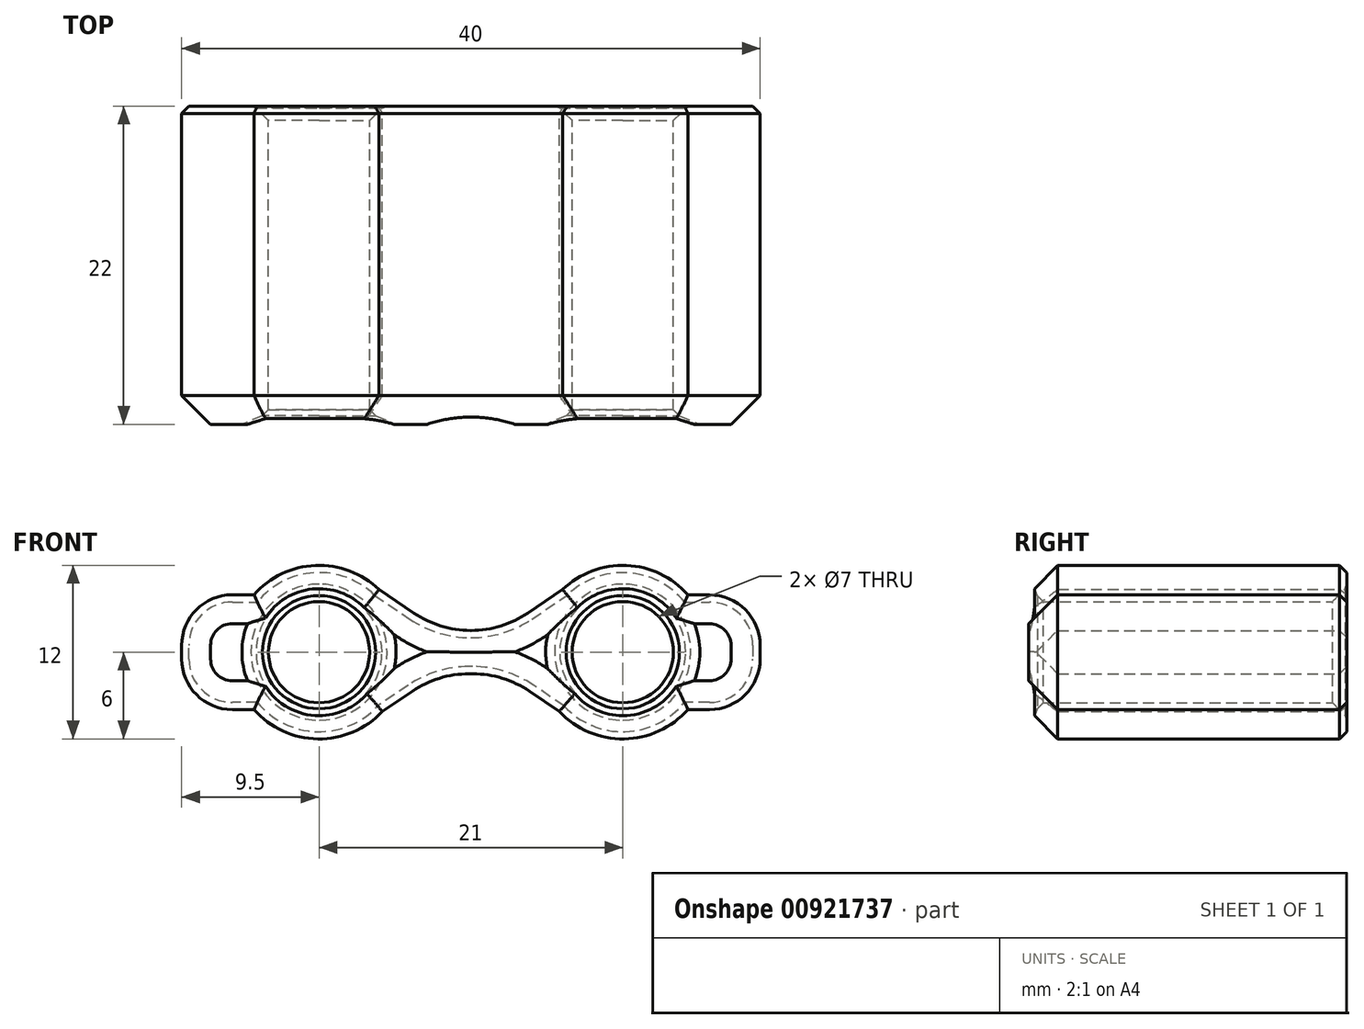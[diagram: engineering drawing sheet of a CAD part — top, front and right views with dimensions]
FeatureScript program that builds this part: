
annotation { "Feature Type Name" : "Feature", "Feature Type Description" : "" }
export const myFeature = defineFeature(function(context is Context, id is Id, definition is map)
    precondition{}
    {
        {
            var Q0;
            Q0=qCreatedBy(makeId("Front.planeOp"),FACE);
            var sketch = newSketch(context, id + "F0", { "sketchPlane" : qUnion([Q0])});
            skPoint(sketch, "E0.middle", {"position": v(0, 0) * mm});
            skArc(sketch, "E1", {"start": v(-15, -3.97) * mm, "mid": v(-10.59, -6) * mm, "end": v(-6.12, -4.1) * mm});
            skArc(sketch, "E2", {"start": v(15, 3.96) * mm, "mid": v(10.76, 6) * mm, "end": v(6.35, 4.33) * mm});
            skLineSegment(sketch, "E3", {"start": v(-15, 3.97) * mm, "end": v(-20, 3.97) * mm});
            skLineSegment(sketch, "E4", {"start": v(-15, -3.97) * mm, "end": v(-20, -3.97) * mm});
            skLineSegment(sketch, "E5", {"start": v(-20, -3.97) * mm, "end": v(-20, 3.97) * mm});
            skLineSegment(sketch, "E6", {"start": v(15, 3.96) * mm, "end": v(20, 3.96) * mm});
            skLineSegment(sketch, "E7", {"start": v(15, -3.97) * mm, "end": v(20, -3.97) * mm});
            skLineSegment(sketch, "E8", {"start": v(20, -3.97) * mm, "end": v(20, 3.96) * mm});
            skCircle(sketch, "E9", {"center": v(-10.5, 0) * mm, "radius": 3.5 * mm});
            skCircle(sketch, "E10", {"center": v(10.5, 0) * mm, "radius": 3.5 * mm});
            skArc(sketch, "E11.trimOffspring", {"start": v(-6.35, 4.33) * mm, "mid": v(-10.75, 6) * mm, "end": v(-15, 3.97) * mm});
            skArc(sketch, "E12.trimOffspring", {"start": v(6.12, -4.1) * mm, "mid": v(10.59, -6) * mm, "end": v(15, -3.97) * mm});
            skLineSegment(sketch, "E13.trimOffspring", {"start": v(2.27, -1.5) * mm, "end": v(-2.27, -1.5) * mm});
            skPoint(sketch, "E14.left.end.orphan", {"position": v(8.46, -1.5) * mm});
            skLineSegment(sketch, "E15.trimOffspring", {"start": v(2.16, 1.5) * mm, "end": v(-2.16, 1.5) * mm});
            skPoint(sketch, "E14.right.end.orphan", {"position": v(-8.46, -1.5) * mm});
            skPoint(sketch, "E14.right.start.orphan", {"position": v(-8.46, 1.5) * mm});
            skPoint(sketch, "E14.bottom.start.orphan", {"position": v(8.46, 1.5) * mm});
            skLineSegment(sketch, "E16", {"start": v(-6.35, 4.33) * mm, "end": v(-2.16, 1.5) * mm});
            skLineSegment(sketch, "E17", {"start": v(6.35, 4.33) * mm, "end": v(2.16, 1.5) * mm});
            skLineSegment(sketch, "E18.trimOffspring", {"start": v(2.27, -1.5) * mm, "end": v(6.12, -4.1) * mm});
            skLineSegment(sketch, "E19.trimOffspring", {"start": v(-2.27, -1.5) * mm, "end": v(-6.12, -4.1) * mm});
            skSolve(sketch);
        }
        {
            var Q0;
            Q0=makeQuery(id+"F0.imprint","IMPRINT",FACE,{"disambiguationData":[TD([[makeQuery(id+"F0.imprint","IMPRINT",EDGE,{"derivedFrom":sQuery(id+"F0.wireOp",EDGE,"E1")}),1.0]])]});
            extrude(context, id + "F1", {"entities" : qUnion([Q0]), "depth" : 22 * mm, "offsetDistance" : 25 * mm});
        }
        {
            var Q0;
            Q0=makeQuery(id+"F1.opExtrude","CAP_EDGE",EDGE,{"disambiguationData":[OSD([sQuery(id+"F0.wireOp",EDGE,"E9")])],"isStart":false});
            var Q1;
            Q1=makeQuery(id+"F1.opExtrude","CAP_EDGE",EDGE,{"disambiguationData":[OSD([sQuery(id+"F0.wireOp",EDGE,"E10")])],"isStart":false});
            var Q2;
            Q2=makeQuery(id+"F1.opExtrude","CAP_EDGE",EDGE,{"disambiguationData":[OSD([sQuery(id+"F0.wireOp",EDGE,"E9")])],"isStart":true});
            var Q3;
            Q3=makeQuery(id+"F1.opExtrude","CAP_EDGE",EDGE,{"disambiguationData":[OSD([sQuery(id+"F0.wireOp",EDGE,"E10")])],"isStart":true});
            chamfer(context, id + "F2", {"entities" : qUnion([Q0, Q1, Q2, Q3]), "width" : 1 * mm, "tangentPropagation" : true});
        }
        {
            var Q0;
            Q0=makeQuery(id+"F1.opExtrude","SWEPT_EDGE",EDGE,{"disambiguationData":[OSD([sQuery(id+"F0.wireOp",EDGE,"E3"),sQuery(id+"F0.wireOp",EDGE,"E5")])]});
            var Q1;
            Q1=makeQuery(id+"F1.opExtrude","SWEPT_EDGE",EDGE,{"disambiguationData":[OSD([sQuery(id+"F0.wireOp",EDGE,"E4"),sQuery(id+"F0.wireOp",EDGE,"E5")])]});
            var Q2;
            Q2=makeQuery(id+"F1.opExtrude","SWEPT_EDGE",EDGE,{"disambiguationData":[OSD([sQuery(id+"F0.wireOp",EDGE,"E6"),sQuery(id+"F0.wireOp",EDGE,"E8")])]});
            var Q3;
            Q3=makeQuery(id+"F1.opExtrude","SWEPT_EDGE",EDGE,{"disambiguationData":[OSD([sQuery(id+"F0.wireOp",EDGE,"E7"),sQuery(id+"F0.wireOp",EDGE,"E8")])]});
            fillet(context, id + "F3", {"entities" : qUnion([Q0, Q1, Q2, Q3]), "radius" : 3.5 * mm, "tangentPropagation" : true, "allowEdgeOverflow" : false});
        }
        {
            var Q0;
            Q0=makeQuery(id+"F1.opExtrude","SWEPT_EDGE",EDGE,{"disambiguationData":[OSD([sQuery(id+"F0.wireOp",EDGE,"E15.trimOffspring"),sQuery(id+"F0.wireOp",EDGE,"E16")])]});
            var Q1;
            Q1=makeQuery(id+"F1.opExtrude","SWEPT_EDGE",EDGE,{"disambiguationData":[OSD([sQuery(id+"F0.wireOp",EDGE,"E15.trimOffspring"),sQuery(id+"F0.wireOp",EDGE,"E17")])]});
            var Q2;
            Q2=makeQuery(id+"F1.opExtrude","SWEPT_EDGE",EDGE,{"disambiguationData":[OSD([sQuery(id+"F0.wireOp",EDGE,"E13.trimOffspring"),sQuery(id+"F0.wireOp",EDGE,"E19.trimOffspring")])]});
            var Q3;
            Q3=makeQuery(id+"F1.opExtrude","SWEPT_EDGE",EDGE,{"disambiguationData":[OSD([sQuery(id+"F0.wireOp",EDGE,"E13.trimOffspring"),sQuery(id+"F0.wireOp",EDGE,"E18.trimOffspring")])]});
            fillet(context, id + "F4", {"entities" : qUnion([Q0, Q1, Q2, Q3]), "radius" : 7 * mm, "tangentPropagation" : true, "allowEdgeOverflow" : false});
        }
        {
            var Q0;
            Q0=makeQuery(id+"F1.opExtrude","CAP_FACE",FACE,{"disambiguationData":[OSD([sQuery(id+"F0.wireOp",EDGE,"E1"),sQuery(id+"F0.wireOp",EDGE,"E2"),sQuery(id+"F0.wireOp",EDGE,"E3"),sQuery(id+"F0.wireOp",EDGE,"E4"),sQuery(id+"F0.wireOp",EDGE,"E5"),sQuery(id+"F0.wireOp",EDGE,"E6"),sQuery(id+"F0.wireOp",EDGE,"E7"),sQuery(id+"F0.wireOp",EDGE,"E8"),sQuery(id+"F0.wireOp",EDGE,"E9"),sQuery(id+"F0.wireOp",EDGE,"E10"),sQuery(id+"F0.wireOp",EDGE,"E11.trimOffspring"),sQuery(id+"F0.wireOp",EDGE,"E12.trimOffspring"),sQuery(id+"F0.wireOp",EDGE,"E13.trimOffspring"),sQuery(id+"F0.wireOp",EDGE,"E15.trimOffspring"),sQuery(id+"F0.wireOp",EDGE,"E16"),sQuery(id+"F0.wireOp",EDGE,"E17"),sQuery(id+"F0.wireOp",EDGE,"E18.trimOffspring"),sQuery(id+"F0.wireOp",EDGE,"E19.trimOffspring")])],"isStart":false});
            chamfer(context, id + "F5", {"entities" : qUnion([Q0]), "width" : 2 * mm, "tangentPropagation" : true});
        }
        {
            var Q0;
            {var subQ0=sQuery(id+"F0.wireOp",EDGE,"E8");var subQ1=sQuery(id+"F0.wireOp",EDGE,"E6");Q0=makeQuery(id+"F3.opFillet","BLEND_EDGE",EDGE,{"blendedFrom":[makeQuery(id+"F1.opExtrude","SWEPT_EDGE",EDGE,{"disambiguationData":[OSD([subQ1,subQ0])]}),makeQuery(id+"F1.opExtrude","CAP_FACE",FACE,{"disambiguationData":[OSD([sQuery(id+"F0.wireOp",EDGE,"E1"),sQuery(id+"F0.wireOp",EDGE,"E2"),sQuery(id+"F0.wireOp",EDGE,"E3"),sQuery(id+"F0.wireOp",EDGE,"E4"),sQuery(id+"F0.wireOp",EDGE,"E5"),subQ1,sQuery(id+"F0.wireOp",EDGE,"E7"),subQ0,sQuery(id+"F0.wireOp",EDGE,"E9"),sQuery(id+"F0.wireOp",EDGE,"E10"),sQuery(id+"F0.wireOp",EDGE,"E11.trimOffspring"),sQuery(id+"F0.wireOp",EDGE,"E12.trimOffspring"),sQuery(id+"F0.wireOp",EDGE,"E13.trimOffspring"),sQuery(id+"F0.wireOp",EDGE,"E15.trimOffspring"),sQuery(id+"F0.wireOp",EDGE,"E16"),sQuery(id+"F0.wireOp",EDGE,"E17"),sQuery(id+"F0.wireOp",EDGE,"E18.trimOffspring"),sQuery(id+"F0.wireOp",EDGE,"E19.trimOffspring")])],"isStart":true})],"blendedInto":[makeQuery(id+"F1.opExtrude","CAP_FACE",FACE,{"disambiguationData":[OSD([sQuery(id+"F0.wireOp",EDGE,"E1"),sQuery(id+"F0.wireOp",EDGE,"E2"),sQuery(id+"F0.wireOp",EDGE,"E3"),sQuery(id+"F0.wireOp",EDGE,"E4"),sQuery(id+"F0.wireOp",EDGE,"E5"),subQ1,sQuery(id+"F0.wireOp",EDGE,"E7"),subQ0,sQuery(id+"F0.wireOp",EDGE,"E9"),sQuery(id+"F0.wireOp",EDGE,"E10"),sQuery(id+"F0.wireOp",EDGE,"E11.trimOffspring"),sQuery(id+"F0.wireOp",EDGE,"E12.trimOffspring"),sQuery(id+"F0.wireOp",EDGE,"E13.trimOffspring"),sQuery(id+"F0.wireOp",EDGE,"E15.trimOffspring"),sQuery(id+"F0.wireOp",EDGE,"E16"),sQuery(id+"F0.wireOp",EDGE,"E17"),sQuery(id+"F0.wireOp",EDGE,"E18.trimOffspring"),sQuery(id+"F0.wireOp",EDGE,"E19.trimOffspring")])],"isStart":true})]});}
            var Q1;
            {var subQ0=sQuery(id+"F0.wireOp",EDGE,"E5");var subQ1=sQuery(id+"F0.wireOp",EDGE,"E3");Q1=makeQuery(id+"F3.opFillet","BLEND_EDGE",EDGE,{"blendedFrom":[makeQuery(id+"F1.opExtrude","SWEPT_EDGE",EDGE,{"disambiguationData":[OSD([subQ1,subQ0])]}),makeQuery(id+"F1.opExtrude","CAP_FACE",FACE,{"disambiguationData":[OSD([sQuery(id+"F0.wireOp",EDGE,"E1"),sQuery(id+"F0.wireOp",EDGE,"E2"),subQ1,sQuery(id+"F0.wireOp",EDGE,"E4"),subQ0,sQuery(id+"F0.wireOp",EDGE,"E6"),sQuery(id+"F0.wireOp",EDGE,"E7"),sQuery(id+"F0.wireOp",EDGE,"E8"),sQuery(id+"F0.wireOp",EDGE,"E9"),sQuery(id+"F0.wireOp",EDGE,"E10"),sQuery(id+"F0.wireOp",EDGE,"E11.trimOffspring"),sQuery(id+"F0.wireOp",EDGE,"E12.trimOffspring"),sQuery(id+"F0.wireOp",EDGE,"E13.trimOffspring"),sQuery(id+"F0.wireOp",EDGE,"E15.trimOffspring"),sQuery(id+"F0.wireOp",EDGE,"E16"),sQuery(id+"F0.wireOp",EDGE,"E17"),sQuery(id+"F0.wireOp",EDGE,"E18.trimOffspring"),sQuery(id+"F0.wireOp",EDGE,"E19.trimOffspring")])],"isStart":true})],"blendedInto":[makeQuery(id+"F1.opExtrude","CAP_FACE",FACE,{"disambiguationData":[OSD([sQuery(id+"F0.wireOp",EDGE,"E1"),sQuery(id+"F0.wireOp",EDGE,"E2"),subQ1,sQuery(id+"F0.wireOp",EDGE,"E4"),subQ0,sQuery(id+"F0.wireOp",EDGE,"E6"),sQuery(id+"F0.wireOp",EDGE,"E7"),sQuery(id+"F0.wireOp",EDGE,"E8"),sQuery(id+"F0.wireOp",EDGE,"E9"),sQuery(id+"F0.wireOp",EDGE,"E10"),sQuery(id+"F0.wireOp",EDGE,"E11.trimOffspring"),sQuery(id+"F0.wireOp",EDGE,"E12.trimOffspring"),sQuery(id+"F0.wireOp",EDGE,"E13.trimOffspring"),sQuery(id+"F0.wireOp",EDGE,"E15.trimOffspring"),sQuery(id+"F0.wireOp",EDGE,"E16"),sQuery(id+"F0.wireOp",EDGE,"E17"),sQuery(id+"F0.wireOp",EDGE,"E18.trimOffspring"),sQuery(id+"F0.wireOp",EDGE,"E19.trimOffspring")])],"isStart":true})]});}
            var Q2;
            Q2=makeQuery(id+"F1.opExtrude","CAP_FACE",FACE,{"disambiguationData":[OSD([sQuery(id+"F0.wireOp",EDGE,"E1"),sQuery(id+"F0.wireOp",EDGE,"E2"),sQuery(id+"F0.wireOp",EDGE,"E3"),sQuery(id+"F0.wireOp",EDGE,"E4"),sQuery(id+"F0.wireOp",EDGE,"E5"),sQuery(id+"F0.wireOp",EDGE,"E6"),sQuery(id+"F0.wireOp",EDGE,"E7"),sQuery(id+"F0.wireOp",EDGE,"E8"),sQuery(id+"F0.wireOp",EDGE,"E9"),sQuery(id+"F0.wireOp",EDGE,"E10"),sQuery(id+"F0.wireOp",EDGE,"E11.trimOffspring"),sQuery(id+"F0.wireOp",EDGE,"E12.trimOffspring"),sQuery(id+"F0.wireOp",EDGE,"E13.trimOffspring"),sQuery(id+"F0.wireOp",EDGE,"E15.trimOffspring"),sQuery(id+"F0.wireOp",EDGE,"E16"),sQuery(id+"F0.wireOp",EDGE,"E17"),sQuery(id+"F0.wireOp",EDGE,"E18.trimOffspring"),sQuery(id+"F0.wireOp",EDGE,"E19.trimOffspring")])],"isStart":true});
            chamfer(context, id + "F6", {"entities" : qUnion([Q0, Q1, Q2]), "width" : 0.5 * mm, "tangentPropagation" : true});
        }
    });
